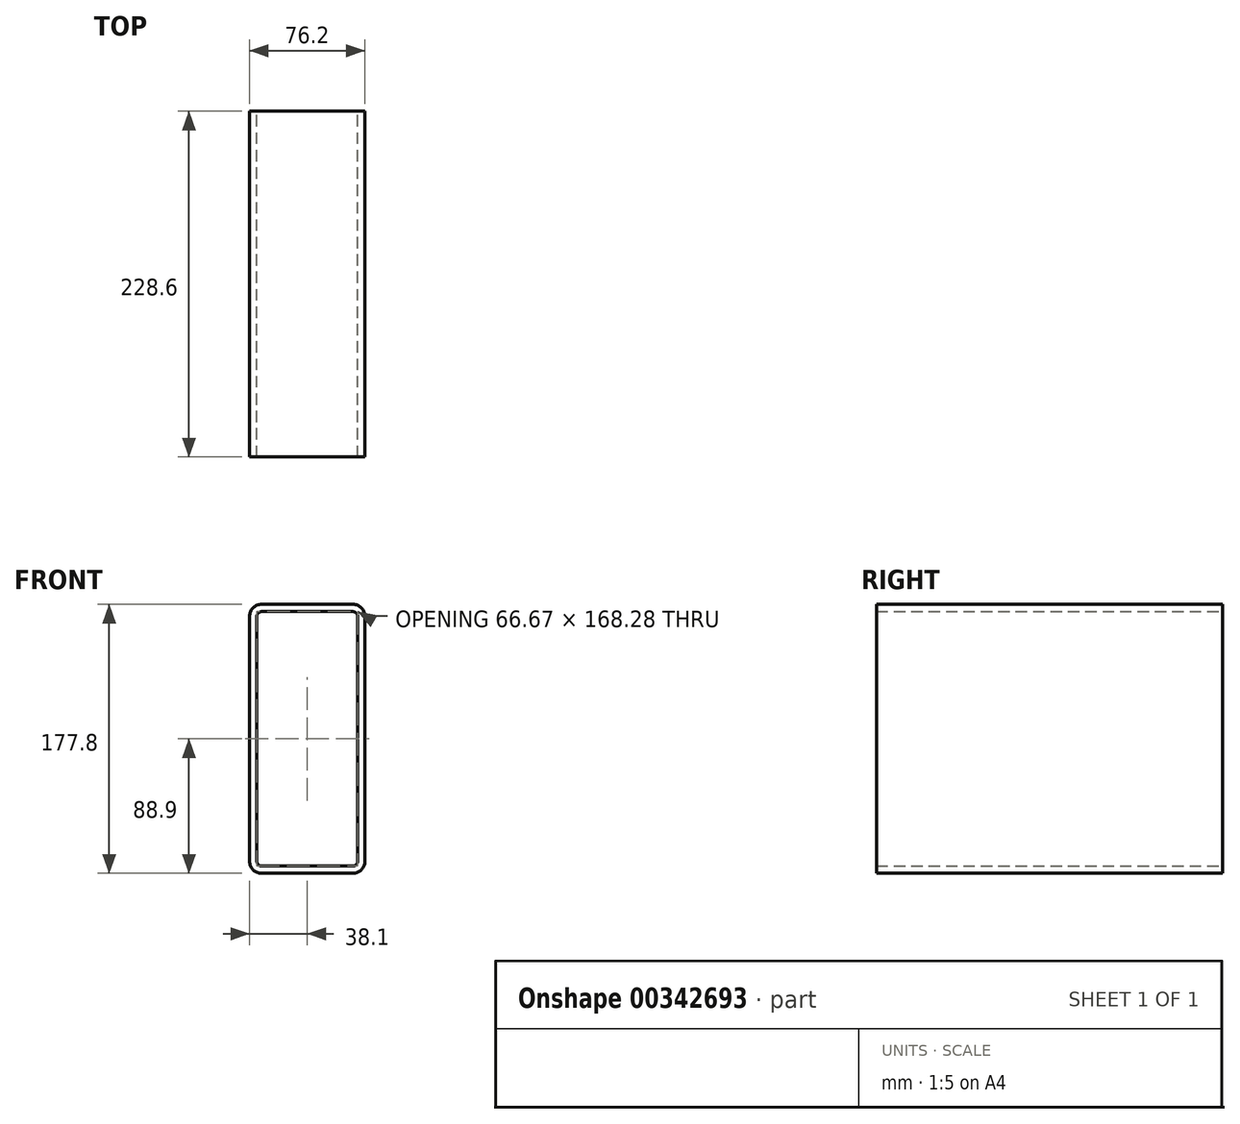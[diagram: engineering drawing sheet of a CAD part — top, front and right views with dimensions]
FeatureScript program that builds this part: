
annotation { "Feature Type Name" : "Feature", "Feature Type Description" : "" }
export const myFeature = defineFeature(function(context is Context, id is Id, definition is map)
    precondition{}
    {
        {
            var Q0;
            Q0=qCreatedBy(makeId("Front.planeOp"),FACE);
            var sketch = newSketch(context, id + "F0", { "sketchPlane" : qUnion([Q0])});
            skLineSegment(sketch, "E0.bottom", {"start": v(30.16, 88.9) * mm, "end": v(-30.16, 88.9) * mm});
            skLineSegment(sketch, "E0.top", {"start": v(30.16, -88.9) * mm, "end": v(-30.16, -88.9) * mm});
            skLineSegment(sketch, "E0.left", {"start": v(38.1, 80.96) * mm, "end": v(38.1, -80.96) * mm});
            skLineSegment(sketch, "E0.right", {"start": v(-38.1, 80.96) * mm, "end": v(-38.1, -80.96) * mm});
            skPoint(sketch, "E0.middle", {"position": v(0, 0) * mm});
            skPoint(sketch, "E1.visualSharp", {"position": v(-38.1, 88.9) * mm});
            skArc(sketch, "E1.filletArc", {"start": v(-30.16, 88.9) * mm, "mid": v(-35.78, 86.58) * mm, "end": v(-38.1, 80.96) * mm});
            skPoint(sketch, "E2.visualSharp", {"position": v(38.1, 88.9) * mm});
            skArc(sketch, "E2.filletArc", {"start": v(38.1, 80.96) * mm, "mid": v(35.78, 86.58) * mm, "end": v(30.16, 88.9) * mm});
            skPoint(sketch, "E3.visualSharp", {"position": v(38.1, -88.9) * mm});
            skArc(sketch, "E3.filletArc", {"start": v(30.16, -88.9) * mm, "mid": v(35.78, -86.58) * mm, "end": v(38.1, -80.96) * mm});
            skPoint(sketch, "E4.visualSharp", {"position": v(-38.1, -88.9) * mm});
            skArc(sketch, "E4.filletArc", {"start": v(-38.1, -80.96) * mm, "mid": v(-35.78, -86.58) * mm, "end": v(-30.16, -88.9) * mm});
            skArc(sketch, "E5.0", {"start": v(-30.16, 84.14) * mm, "mid": v(-32.4, 83.2) * mm, "end": v(-33.34, 80.96) * mm});
            skLineSegment(sketch, "E5.1", {"start": v(30.16, 84.14) * mm, "end": v(-30.16, 84.14) * mm});
            skLineSegment(sketch, "E5.2", {"start": v(-33.34, 80.96) * mm, "end": v(-33.34, -80.96) * mm});
            skArc(sketch, "E5.3", {"start": v(33.34, 80.96) * mm, "mid": v(32.4, 83.2) * mm, "end": v(30.16, 84.14) * mm});
            skArc(sketch, "E5.4", {"start": v(-33.34, -80.96) * mm, "mid": v(-32.4, -83.2) * mm, "end": v(-30.16, -84.14) * mm});
            skLineSegment(sketch, "E5.5", {"start": v(30.16, -84.14) * mm, "end": v(-30.16, -84.14) * mm});
            skArc(sketch, "E5.6", {"start": v(30.16, -84.14) * mm, "mid": v(32.4, -83.2) * mm, "end": v(33.34, -80.96) * mm});
            skLineSegment(sketch, "E5.7", {"start": v(33.34, 80.96) * mm, "end": v(33.34, -80.96) * mm});
            skSolve(sketch);
        }
        {
            var Q0;
            Q0=makeQuery(id+"F0.imprint","IMPRINT",FACE,{"disambiguationData":[TD([[makeQuery(id+"F0.imprint","IMPRINT",EDGE,{"derivedFrom":sQuery(id+"F0.wireOp",EDGE,"E0.bottom")}),1.0]])]});
            extrude(context, id + "F1", {"entities" : qUnion([Q0]), "depth" : 228.6 * mm});
        }
    });
